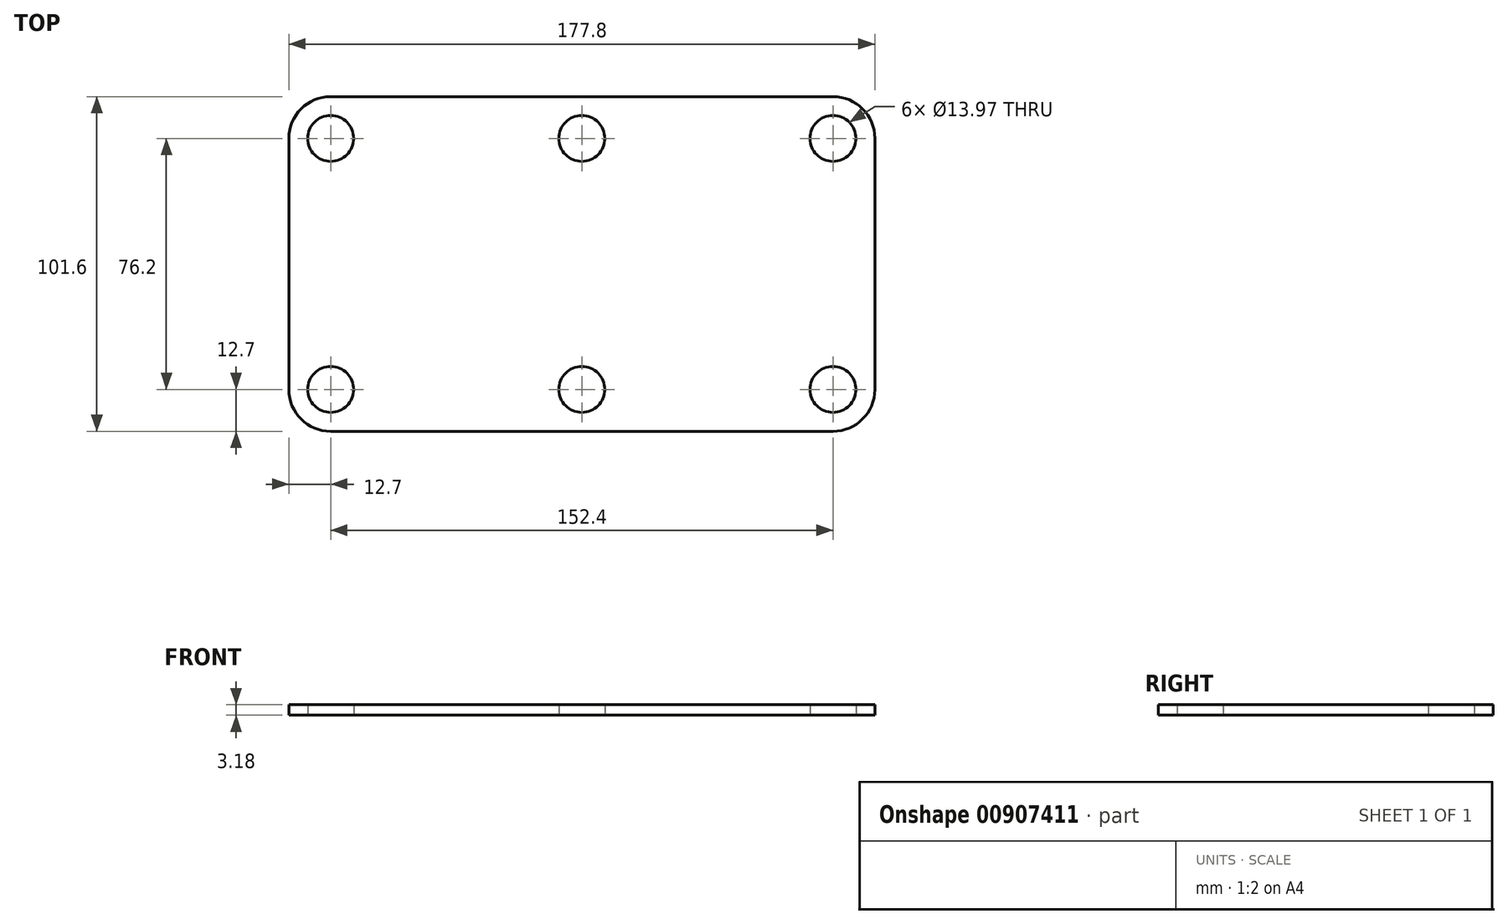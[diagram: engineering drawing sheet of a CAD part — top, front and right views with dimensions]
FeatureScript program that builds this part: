
annotation { "Feature Type Name" : "Feature", "Feature Type Description" : "" }
export const myFeature = defineFeature(function(context is Context, id is Id, definition is map)
    precondition{}
    {
        {
            var Q0;
            Q0=qCreatedBy(makeId("Top.planeOp"),FACE);
            var sketch = newSketch(context, id + "F0", { "sketchPlane" : qUnion([Q0])});
            skCircle(sketch, "E0", {"center": v(0, 76.2) * mm, "radius": 6.99 * mm});
            skCircle(sketch, "E1", {"center": v(76.2, 76.2) * mm, "radius": 6.99 * mm});
            skCircle(sketch, "E2", {"center": v(76.2, 0) * mm, "radius": 6.99 * mm});
            skCircle(sketch, "E3", {"center": v(0, 0) * mm, "radius": 6.99 * mm});
            skLineSegment(sketch, "E4.1", {"start": v(-12.7, 0) * mm, "end": v(-12.7, 76.2) * mm});
            skPoint(sketch, "E5.visualSharp", {"position": v(-12.7, 88.9) * mm});
            skArc(sketch, "E5.filletArc", {"start": v(0, 88.9) * mm, "mid": v(-8.98, 85.18) * mm, "end": v(-12.7, 76.2) * mm});
            skPoint(sketch, "E6.visualSharp", {"position": v(-12.7, -12.7) * mm});
            skArc(sketch, "E6.filletArc", {"start": v(-12.7, 0) * mm, "mid": v(-8.98, -8.98) * mm, "end": v(0, -12.7) * mm});
            skLineSegment(sketch, "E7.MirrorCS", {"start": v(165.1, 0) * mm, "end": v(165.1, 76.2) * mm});
            skPoint(sketch, "E8.MirrorP", {"position": v(165.1, 88.9) * mm});
            skPoint(sketch, "E9.MirrorP", {"position": v(165.1, -12.7) * mm});
            skArc(sketch, "E10.MirrorCS", {"start": v(165.1, 0) * mm, "mid": v(161.38, -8.98) * mm, "end": v(152.4, -12.7) * mm});
            skCircle(sketch, "E11.MirrorC", {"center": v(152.4, 0) * mm, "radius": 6.99 * mm});
            skArc(sketch, "E12.MirrorCS", {"start": v(152.4, 88.9) * mm, "mid": v(161.38, 85.18) * mm, "end": v(165.1, 76.2) * mm});
            skCircle(sketch, "E13.MirrorC", {"center": v(152.4, 76.2) * mm, "radius": 6.99 * mm});
            skLineSegment(sketch, "E14", {"start": v(0, 88.9) * mm, "end": v(152.4, 88.9) * mm});
            skLineSegment(sketch, "E15", {"start": v(0, -12.7) * mm, "end": v(152.4, -12.7) * mm});
            skSolve(sketch);
        }
        {
            var Q0;
            Q0 = qSketchRegion(id + "F0", true);
            extrude(context, id + "F1", {"entities" : qUnion([Q0]), "depth" : 3.17 * mm, "offsetDistance" : 25.4 * mm});
        }
    });
